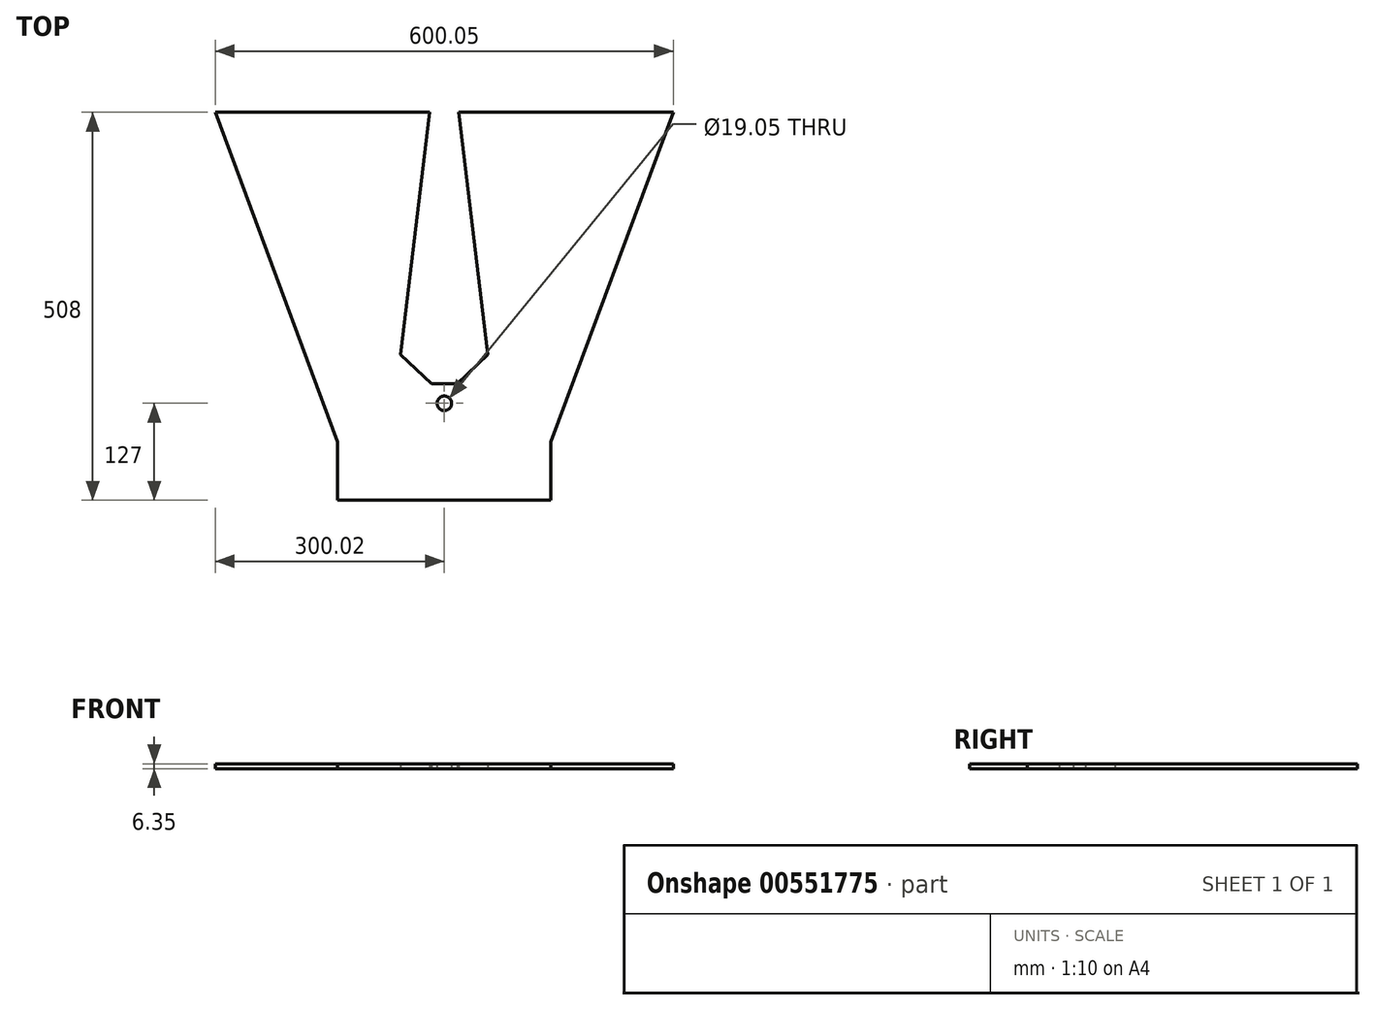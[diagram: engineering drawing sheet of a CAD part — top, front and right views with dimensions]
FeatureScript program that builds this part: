
annotation { "Feature Type Name" : "Feature", "Feature Type Description" : "" }
export const myFeature = defineFeature(function(context is Context, id is Id, definition is map)
    precondition{}
    {
        {
            var Q0;
            Q0=qCreatedBy(makeId("Top.planeOp"),FACE);
            var sketch = newSketch(context, id + "F0", { "sketchPlane" : qUnion([Q0])});
            skLineSegment(sketch, "E0", {"start": v(0, 0) * mm, "end": v(-139.7, 0) * mm});
            skLineSegment(sketch, "E1", {"start": v(0, 0) * mm, "end": v(139.7, 0) * mm});
            skPoint(sketch, "E2", {"position": v(0, 381) * mm});
            skLineSegment(sketch, "E3", {"start": v(0, 381) * mm, "end": v(-883.72, 381) * mm, "construction": true});
            skLineSegment(sketch, "E4", {"start": v(0, 381) * mm, "end": v(761.76, 381) * mm, "construction": true});
            skLineSegment(sketch, "E5", {"start": v(-19.05, 508) * mm, "end": v(-300.02, 508) * mm});
            skLineSegment(sketch, "E6", {"start": v(19.05, 508) * mm, "end": v(300.03, 508) * mm});
            skLineSegment(sketch, "E7", {"start": v(0, 152.4) * mm, "end": v(16.93, 152.4) * mm});
            skLineSegment(sketch, "E8", {"start": v(16.93, 152.4) * mm, "end": v(-16.93, 152.4) * mm});
            skLineSegment(sketch, "E9", {"start": v(-16.93, 152.4) * mm, "end": v(-57.15, 190.5) * mm});
            skLineSegment(sketch, "E10", {"start": v(16.93, 152.4) * mm, "end": v(57.15, 190.5) * mm});
            skLineSegment(sketch, "E11", {"start": v(-19.05, 508) * mm, "end": v(-57.15, 190.5) * mm});
            skLineSegment(sketch, "E12", {"start": v(57.15, 190.5) * mm, "end": v(19.45, 504.7) * mm});
            skLineSegment(sketch, "E13", {"start": v(-139.7, 0) * mm, "end": v(-139.7, 76.2) * mm});
            skLineSegment(sketch, "E14", {"start": v(139.7, 0) * mm, "end": v(139.7, 76.2) * mm});
            skLineSegment(sketch, "E15", {"start": v(139.7, 76.2) * mm, "end": v(300.03, 508) * mm});
            skLineSegment(sketch, "E16", {"start": v(-300.02, 508) * mm, "end": v(-139.7, 76.2) * mm});
            skLineSegment(sketch, "E17", {"start": v(0, 0) * mm, "end": v(0, 127) * mm});
            skCircle(sketch, "E18", {"center": v(0, 127) * mm, "radius": 9.53 * mm});
            skPoint(sketch, "E19.visualSharp", {"position": v(19.05, 508) * mm});
            skLineSegment(sketch, "E20", {"start": v(19.05, 508) * mm, "end": v(19.45, 504.7) * mm});
            skLineSegment(sketch, "E21", {"start": v(19.05, 508) * mm, "end": v(19.05, 508) * mm});
            skLineSegment(sketch, "E22", {"start": v(0, 152.4) * mm, "end": v(0, 524.97) * mm});
            skSolve(sketch);
        }
        {
            var Q0;
            Q0=makeQuery(id+"F0.imprint","IMPRINT",FACE,{"disambiguationData":[TD([[makeQuery(id+"F0.imprint","IMPRINT",EDGE,{"derivedFrom":sQuery(id+"F0.wireOp",EDGE,"E0")}),-1.0]])]});
            var Q1;
            Q1=makeQuery(id+"F0.imprint","IMPRINT",FACE,{"disambiguationData":[TD([[makeQuery(id+"F0.imprint","IMPRINT",EDGE,{"derivedFrom":sQuery(id+"F0.wireOp",EDGE,"E1")}),1.0]])]});
            extrude(context, id + "F1", {"entities" : qUnion([Q0, Q1]), "depth" : 6.35 * mm, "offsetDistance" : 25.4 * mm});
        }
    });
